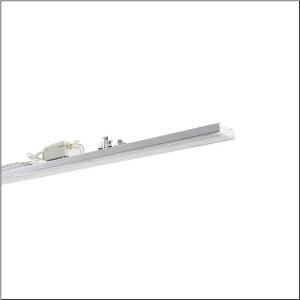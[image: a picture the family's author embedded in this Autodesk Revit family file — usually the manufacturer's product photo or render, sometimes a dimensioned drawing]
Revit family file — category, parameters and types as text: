
# Revit family: licross_r__21_recessed_ho_52tl12dn4fxm3c_2914
name_source: partatom
category: Lighting Fixtures
units: mm (PartAtom-declared; Revit-internal decimal feet)

## family parameters
Cut with Voids When Loaded = No
Host = Face
Light Source = No
Part Type = Normal
Room Calculation Point = No
Round Connector Dimension = Use Diameter
Shared = No

## types (1)
- --- (1 x LED, 930 lm, 7.5 W, 4000K)
    Apparent Load = 8 VA
    CIE Flux Codes = 69 91 98 100 100
    Color Rendering = 80
    Color Temperature = 4000K
    Default Elevation = 1800 mm
    Description = Licross® 21 Recessed HO, luminaire insert, of sheet steel, galvanised, coil coated, white, length: 1.500mm, width: 66mm, height: 67mm, LED rated luminous flux: 15.000lm, light colour: 840, control gear: DALI 2, with plug, 6-pole, with phase selection, for trunking rail, 14-core, mains connection: 220..240V, AC, 50/60Hz, rated input power: 88W, halogen-free wiring, for emergency light function, for trunking rail, 14-core, converter,control gear: single battery element, battery: LiFeP04, 9Ah, primary optical cover: cover, of PMMA, light emission: direct distribution, primary light characteristic: symmetric, protection rating (complete): IP40, insulation class (complete): insulation class I (protective earthing), certification: CE, UKCA, protection symbol: D if used in an environment without relevant dust loads with corresponding accessories, impact resistance: IK06, permissible ambient temperature for indoor applications: +5..+30°C, standard: EN 60598-2-22, LABS conformity tested according to VDMA 24364:2018-05, reducing of maximum allowable ambient temperature of 5°C with ceiling mounting, corresponds to IFS (International Featured Standards) requirements for safety and quality in the food industry, packaging unit: 1 piece
    Height = 58 mm
    Lamp = 1 x LED
    Lamp Light Flux = 930 lm
    Lamp Power = 7.5 W
    Lamp count = 1
    Length = 1500 mm
    Luminous efficacy = 124 lm/W
    Manufacturer = Siteco
    ModVariant = No
    Model = 52TL12DN4FXM3C
    Mounting Place = Ceiling
    Mounting Type = Pendant
    Number of Poles = 1
    OnlyDefault = Yes
    Power Factor = 1
    Product Name = Licross® 21 Recessed HO
    Product group = luminaire insert
    ProductGroupID = 901
    Protection Class = Protection class I
    Protection Degree = IP 40
    RLX_Detail_Level = 1
    RLX_Emergency_Light_Flux = 0 lm
    RLX_Emergency_Type = 0
    RLX_Emergency_Type_DB = No
    RlxData = <blob elided: 25061 chars, md5=6df7aa71>
    Socket = socket
    Standby Power = 0 W
    System Light Flux = 930 lm
    System Power = 8 W
    Type Comments = : emergency light operation: 3 h
    Type Image = l_1296930.jpg
    URL = http://relux.com
    VarID = @adj_039447
    Voltage = 0 V
    Weight = 0.00 kg
    Width = 66 mm

## geometry (parser evidence)
native form markers: Blend x4, Sweep x12
no freeform markers — native parametric forms only
